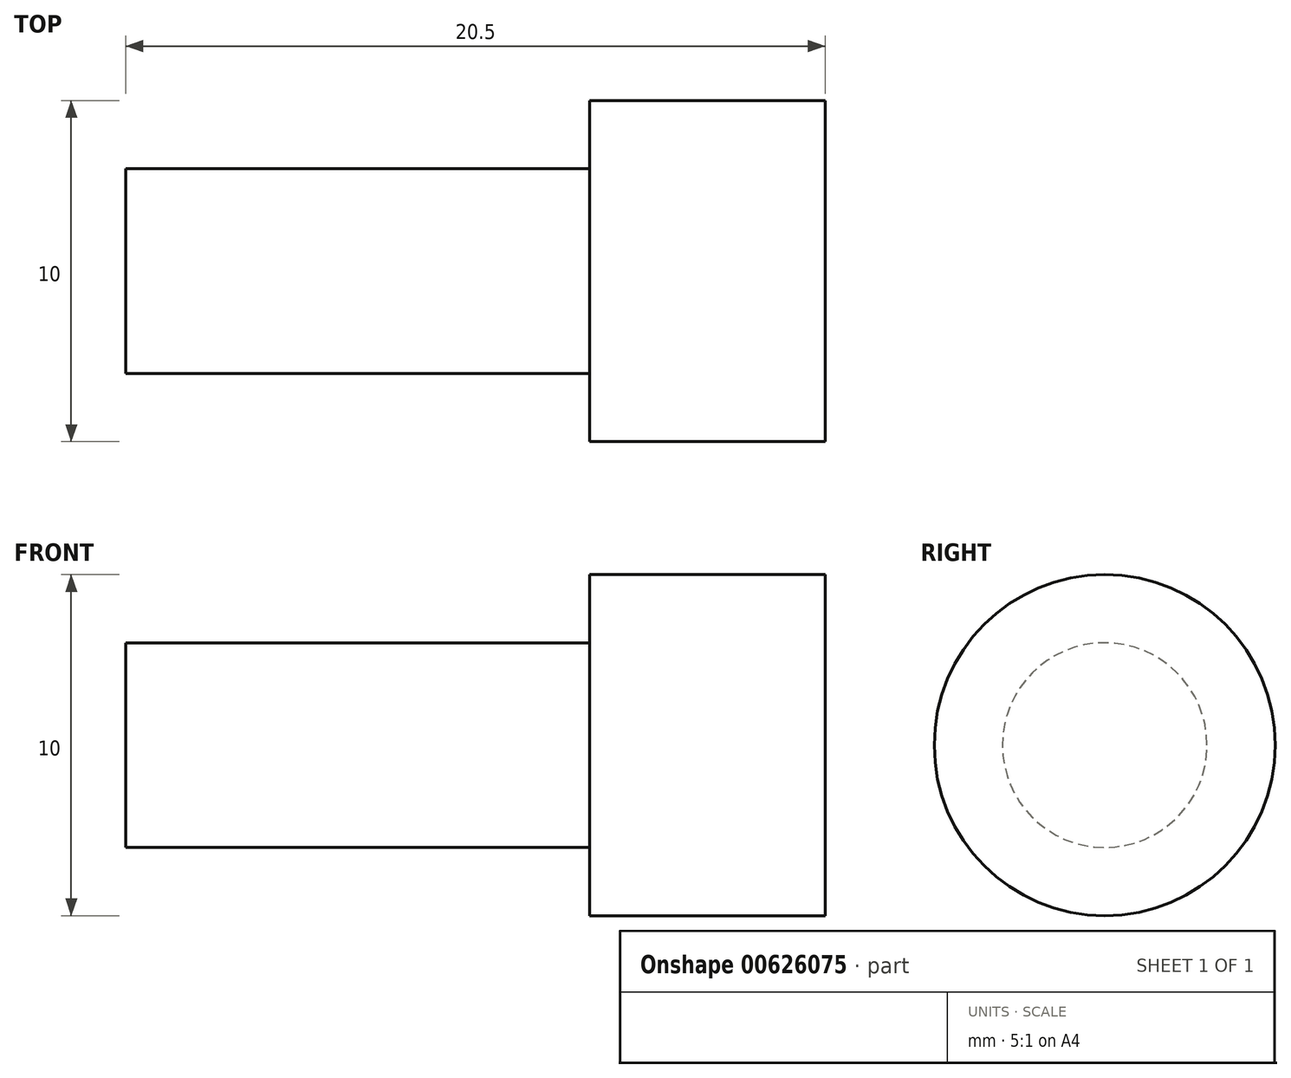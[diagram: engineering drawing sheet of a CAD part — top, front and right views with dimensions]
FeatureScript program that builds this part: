
annotation { "Feature Type Name" : "Feature", "Feature Type Description" : "" }
export const myFeature = defineFeature(function(context is Context, id is Id, definition is map)
    precondition{}
    {
        {
            var Q0;
            Q0=qCreatedBy(makeId("Front.planeOp"),FACE);
            var sketch = newSketch(context, id + "F0", { "sketchPlane" : qUnion([Q0])});
            skLineSegment(sketch, "E0", {"start": v(-20.5, 0) * mm, "end": v(0, 0) * mm});
            skLineSegment(sketch, "E1", {"start": v(0, 0) * mm, "end": v(0, 5) * mm});
            skLineSegment(sketch, "E2", {"start": v(0, 5) * mm, "end": v(-6.9, 5) * mm});
            skLineSegment(sketch, "E3", {"start": v(-6.9, 5) * mm, "end": v(-6.9, 3) * mm});
            skLineSegment(sketch, "E4", {"start": v(-6.9, 3) * mm, "end": v(-20.5, 3) * mm});
            skLineSegment(sketch, "E5", {"start": v(-20.5, 3) * mm, "end": v(-20.5, 0) * mm});
            skSolve(sketch);
        }
        {
            var Q0;
            Q0=makeQuery(id+"F0.imprint","IMPRINT",FACE,{"disambiguationData":[TD([[makeQuery(id+"F0.imprint","IMPRINT",EDGE,{"derivedFrom":sQuery(id+"F0.wireOp",EDGE,"E0")}),1.0]])]});
            var Q1;
            Q1=sQuery(id+"F0.wireOp",EDGE,"E0");
            revolve(context, id + "F1", {"surfaceOperationType" : NewSurfaceOperationType.NEW, "entities" : qUnion([Q0]), "axis" : qUnion([Q1]), "revolveType" : RevolveType.FULL});
        }
    });
